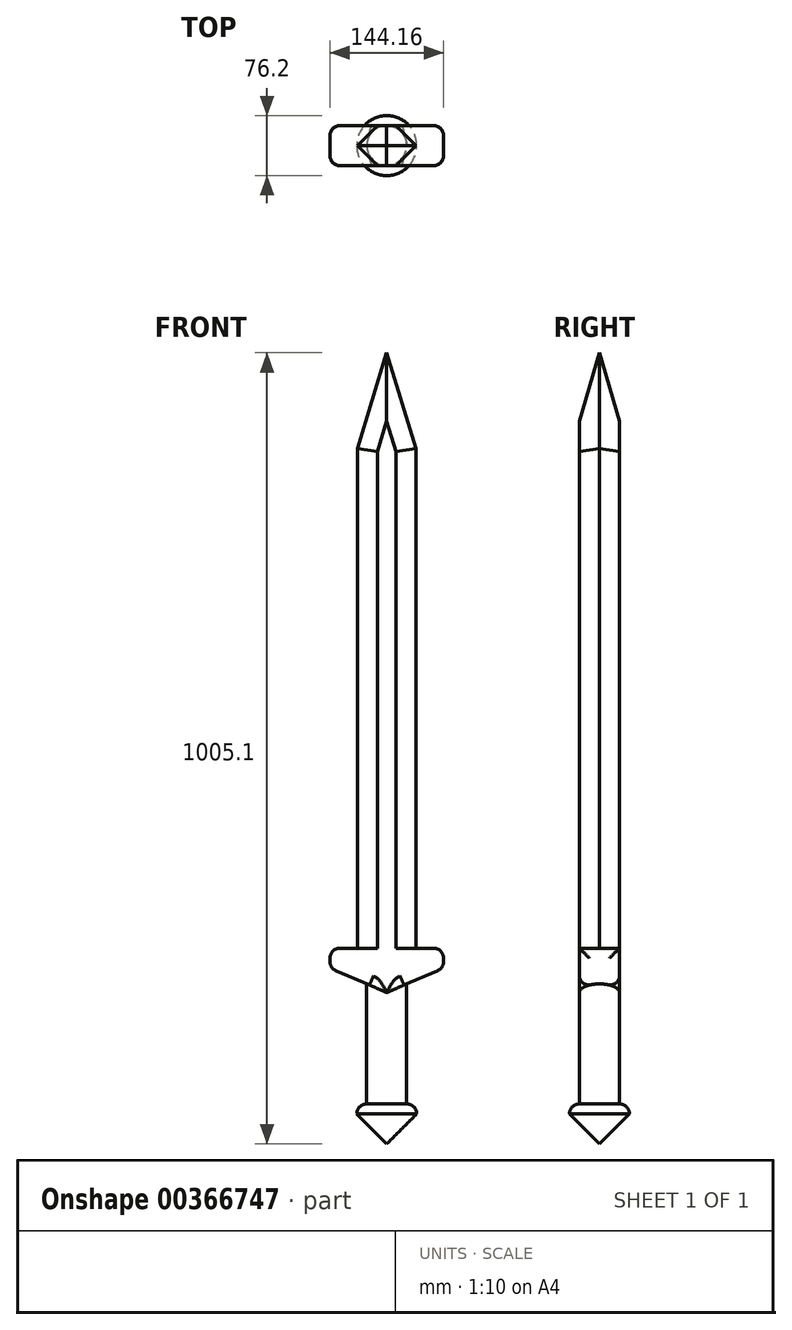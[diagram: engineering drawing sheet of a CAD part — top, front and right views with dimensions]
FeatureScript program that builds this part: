
annotation { "Feature Type Name" : "Feature", "Feature Type Description" : "" }
export const myFeature = defineFeature(function(context is Context, id is Id, definition is map)
    precondition{}
    {
        {
            var Q0;
            Q0=qCreatedBy(makeId("Front.planeOp"),FACE);
            var sketch = newSketch(context, id + "F0", { "sketchPlane" : qUnion([Q0])});
            skLineSegment(sketch, "E0.bottom", {"start": v(25.4, -76.2) * mm, "end": v(-25.4, -76.2) * mm});
            skLineSegment(sketch, "E0.top", {"start": v(25.4, 76.2) * mm, "end": v(-25.4, 76.2) * mm});
            skLineSegment(sketch, "E0.left", {"start": v(25.4, -76.2) * mm, "end": v(25.4, 76.2) * mm});
            skLineSegment(sketch, "E0.right", {"start": v(-25.4, -76.2) * mm, "end": v(-25.4, 76.2) * mm});
            skPoint(sketch, "E0.middle", {"position": v(0, 0) * mm});
            skSolve(sketch);
        }
        {
            var Q0;
            Q0 = qSketchRegion(id + "F0", true);
            extrude(context, id + "F1", {"entities" : qUnion([Q0]), "depth" : 50.8 * mm});
        }
        {
            var Q0;
            Q0=makeQuery(id+"F1.opExtrude","SWEPT_FACE",FACE,{"disambiguationData":[OSD([sQuery(id+"F0.wireOp",EDGE,"E0.bottom")])]});
            var sketch = newSketch(context, id + "F2", { "sketchPlane" : qUnion([Q0])});
            skLineSegment(sketch, "E1", {"start": v(0, 0) * mm, "end": v(0, 50.8) * mm});
            skLineSegment(sketch, "E2", {"start": v(0, 50.8) * mm, "end": v(0, 25.4) * mm});
            skCircle(sketch, "E3", {"center": v(0, 25.4) * mm, "radius": 38.1 * mm});
            skSolve(sketch);
        }
        {
            var Q0;
            Q0 = qSketchRegion(id + "F2", true);
            extrude(context, id + "F3", {"entities" : qUnion([Q0]), "operationType" : NewBodyOperationType.ADD, "depth" : 50.8 * mm});
        }
        {
            var Q0;
            Q0=makeQuery(id+"F1.opExtrude","CAP_FACE",FACE,{"disambiguationData":[OSD([sQuery(id+"F0.wireOp",EDGE,"E0.bottom"),sQuery(id+"F0.wireOp",EDGE,"E0.top"),sQuery(id+"F0.wireOp",EDGE,"E0.left"),sQuery(id+"F0.wireOp",EDGE,"E0.right")])],"isStart":false});
            var sketch = newSketch(context, id + "F4", { "sketchPlane" : qUnion([Q0])});
            skLineSegment(sketch, "E4", {"start": v(-25.4, 76.2) * mm, "end": v(-72.08, 96.23) * mm});
            skLineSegment(sketch, "E5", {"start": v(-72.08, 96.23) * mm, "end": v(-72.08, 121.63) * mm});
            skLineSegment(sketch, "E6", {"start": v(-72.08, 121.63) * mm, "end": v(0, 121.63) * mm});
            skLineSegment(sketch, "E7.MirrorCS", {"start": v(72.08, 121.63) * mm, "end": v(0, 121.63) * mm});
            skLineSegment(sketch, "E8.MirrorCS", {"start": v(72.08, 96.23) * mm, "end": v(72.08, 121.63) * mm});
            skLineSegment(sketch, "E9.MirrorCS", {"start": v(25.4, 76.2) * mm, "end": v(72.08, 96.23) * mm});
            skSolve(sketch);
        }
        {
            var Q0;
            Q0 = qSketchRegion(id + "F4", true);
            var Q1;
            Q1=makeQuery(id+"F4.imprint","IMPRINT",FACE,{"disambiguationData":[TD([[makeQuery(id+"F4.imprint","IMPRINT",EDGE,{"derivedFrom":sQuery(id+"F4.wireOp",EDGE,"E4")}),-1.0]])]});
            extrude(context, id + "F5", {"entities" : qUnion([Q0, Q1]), "operationType" : NewBodyOperationType.ADD, "depth" : -50.8 * mm});
        }
        {
            var Q0;
            {var subQ0=sQuery(id+"F0.wireOp",EDGE,"E0.top");Q0=makeQuery(id+"F5.boolean.opBoolean","MERGE",FACE,{"derivedFrom":[makeQuery(id+"F1.opExtrude","CAP_FACE",FACE,{"disambiguationData":[OSD([sQuery(id+"F0.wireOp",EDGE,"E0.bottom"),subQ0,sQuery(id+"F0.wireOp",EDGE,"E0.left"),sQuery(id+"F0.wireOp",EDGE,"E0.right")])],"isStart":true}),makeQuery(id+"F5.opExtrude","CAP_FACE",FACE,{"disambiguationData":[OSD([subQ0,sQuery(id+"F4.wireOp",EDGE,"E4"),sQuery(id+"F4.wireOp",EDGE,"E5"),sQuery(id+"F4.wireOp",EDGE,"E6"),sQuery(id+"F4.wireOp",EDGE,"E7.MirrorCS"),sQuery(id+"F4.wireOp",EDGE,"E8.MirrorCS"),sQuery(id+"F4.wireOp",EDGE,"E9.MirrorCS")])],"isStart":false})]});}
            var sketch = newSketch(context, id + "F6", { "sketchPlane" : qUnion([Q0])});
            skLineSegment(sketch, "E10", {"start": v(-25.4, 76.2) * mm, "end": v(-25.4, 121.63) * mm});
            skLineSegment(sketch, "E11", {"start": v(25.4, 76.2) * mm, "end": v(25.4, 121.63) * mm});
            skLineSegment(sketch, "E12", {"start": v(-25.4, 121.63) * mm, "end": v(-72.08, 121.63) * mm});
            skLineSegment(sketch, "E13", {"start": v(-72.08, 121.63) * mm, "end": v(-48.74, 121.63) * mm});
            skLineSegment(sketch, "E14", {"start": v(-48.74, 121.63) * mm, "end": v(25.4, 121.63) * mm});
            skLineSegment(sketch, "E15", {"start": v(25.4, 121.63) * mm, "end": v(72.08, 121.63) * mm});
            skLineSegment(sketch, "E16", {"start": v(72.08, 121.63) * mm, "end": v(48.74, 121.63) * mm});
            skLineSegment(sketch, "E17", {"start": v(25.4, 121.63) * mm, "end": v(48.74, 121.63) * mm});
            skLineSegment(sketch, "E18", {"start": v(37.07, 121.63) * mm, "end": v(-25.4, 121.63) * mm});
            skLineSegment(sketch, "E19", {"start": v(-25.4, 121.63) * mm, "end": v(-48.74, 121.63) * mm});
            skLineSegment(sketch, "E20", {"start": v(-48.74, 121.63) * mm, "end": v(-37.07, 121.63) * mm});
            skLineSegment(sketch, "E21", {"start": v(-37.07, 121.63) * mm, "end": v(-25.4, 121.63) * mm});
            skLineSegment(sketch, "E22", {"start": v(-37.07, 121.63) * mm, "end": v(-37.07, 756.63) * mm});
            skLineSegment(sketch, "E23", {"start": v(-37.07, 756.63) * mm, "end": v(0, 878.1) * mm});
            skLineSegment(sketch, "E24.MirrorCS", {"start": v(37.07, 756.63) * mm, "end": v(0, 878.1) * mm});
            skLineSegment(sketch, "E25.MirrorCS", {"start": v(37.07, 121.63) * mm, "end": v(37.07, 756.63) * mm});
            skSolve(sketch);
        }
        {
            var Q0;
            {var subQ0=sQuery(id+"F6.wireOp",EDGE,"PY2WEZBQ-7PR6-9Fpz-Vapi-aHdPcGGFADP5");Q0=makeQuery(id+"F6.imprint","IMPRINT",FACE,{"disambiguationData":[TD([[makeQuery(id+"F6.imprint","IMPRINT",EDGE,{"derivedFrom":subQ0}),-1.0]])]});}
            var Q1;
            {var subQ0=sQuery(id+"F6.wireOp",EDGE,"f0GTGxwF-IPFW-NOuP-a3Bc-MOuoexxvz6AO");Q1=makeQuery(id+"F6.imprint","IMPRINT",FACE,{"disambiguationData":[TD([[makeQuery(id+"F6.imprint","IMPRINT",EDGE,{"derivedFrom":subQ0}),-1.0]])]});}
            var Q2;
            {var subQ1=sQuery(id+"F6.wireOp",EDGE,"6nlB1FJk-VPpw-S0uW-v87S-9lklJtyhY6W3");Q2=makeQuery(id+"F6.imprint","IMPRINT",FACE,{"disambiguationData":[TD([[makeQuery(id+"F6.imprint","IMPRINT",EDGE,{"derivedFrom":subQ1}),1.0]])]});}
            var Q3;
            {var subQ0=sQuery(id+"F6.wireOp",EDGE,"Ocn70z9U-hdZD-j4XZ-LXAR-4gYBC23h8k5L");Q3=makeQuery(id+"F6.imprint","IMPRINT",FACE,{"disambiguationData":[TD([[makeQuery(id+"F6.imprint","IMPRINT",EDGE,{"derivedFrom":subQ0}),-1.0]])]});}
            var Q4;
            {var subQ1=sQuery(id+"F6.wireOp",EDGE,"E15");Q4=makeQuery(id+"F6.imprint","IMPRINT",FACE,{"disambiguationData":[TD([[makeQuery(id+"F6.imprint","IMPRINT",EDGE,{"derivedFrom":subQ1}),1.0]])]});}
            var Q5;
            {var subQ0=sQuery(id+"F6.wireOp",EDGE,"E21");Q5=makeQuery(id+"F6.imprint","IMPRINT",FACE,{"disambiguationData":[TD([[makeQuery(id+"F6.imprint","IMPRINT",EDGE,{"derivedFrom":subQ0}),1.0]])]});}
            extrude(context, id + "F7", {"entities" : qUnion([Q0, Q1, Q2, Q3, Q4, Q5]), "operationType" : NewBodyOperationType.ADD, "depth" : -50.8 * mm});
        }
        {
            var Q0;
            Q0=makeQuery(id+"F1.opExtrude","CAP_EDGE",EDGE,{"disambiguationData":[OSD([sQuery(id+"F0.wireOp",EDGE,"E0.right")])],"isStart":false});
            var Q1;
            Q1=makeQuery(id+"F1.opExtrude","CAP_EDGE",EDGE,{"disambiguationData":[OSD([sQuery(id+"F0.wireOp",EDGE,"E0.left")])],"isStart":false});
            var Q2;
            Q2=makeQuery(id+"F1.opExtrude","CAP_EDGE",EDGE,{"disambiguationData":[OSD([sQuery(id+"F0.wireOp",EDGE,"E0.left")])],"isStart":true});
            var Q3;
            Q3=makeQuery(id+"F1.opExtrude","CAP_EDGE",EDGE,{"disambiguationData":[OSD([sQuery(id+"F0.wireOp",EDGE,"E0.right")])],"isStart":true});
            fillet(context, id + "F8", {"entities" : qUnion([Q0, Q1, Q2, Q3]), "radius" : 25.4 * mm, "tangentPropagation" : true, "allowEdgeOverflow" : false});
        }
        {
            var Q0;
            Q0=makeQuery(id+"F3.opExtrude","CAP_EDGE",EDGE,{"disambiguationData":[OSD([sQuery(id+"F2.wireOp",EDGE,"E3")])],"isStart":true});
            fillet(context, id + "F9", {"entities" : qUnion([Q0]), "radius" : 12.7 * mm, "tangentPropagation" : true, "allowEdgeOverflow" : false});
        }
        {
            var Q0;
            Q0=makeQuery(id+"F3.opExtrude","CAP_EDGE",EDGE,{"disambiguationData":[OSD([sQuery(id+"F2.wireOp",EDGE,"E3")])],"isStart":false});
            chamfer(context, id + "F10", {"entities" : qUnion([Q0]), "width" : 38.1 * mm, "tangentPropagation" : true});
        }
        {
            var Q0;
            Q0=makeQuery(id+"F5.opExtrude","CAP_EDGE",EDGE,{"disambiguationData":[OSD([sQuery(id+"F4.wireOp",EDGE,"E5")])],"isStart":true});
            var Q1;
            Q1=makeQuery(id+"F5.opExtrude","CAP_EDGE",EDGE,{"disambiguationData":[OSD([sQuery(id+"F4.wireOp",EDGE,"E5")])],"isStart":false});
            var Q2;
            Q2=makeQuery(id+"F5.opExtrude","CAP_EDGE",EDGE,{"disambiguationData":[OSD([sQuery(id+"F4.wireOp",EDGE,"E8.MirrorCS")])],"isStart":true});
            var Q3;
            Q3=makeQuery(id+"F5.opExtrude","CAP_EDGE",EDGE,{"disambiguationData":[OSD([sQuery(id+"F4.wireOp",EDGE,"E8.MirrorCS")])],"isStart":false});
            var Q4;
            Q4=makeQuery(id+"F5.opExtrude","SWEPT_EDGE",EDGE,{"disambiguationData":[OSD([sQuery(id+"F4.wireOp",EDGE,"E8.MirrorCS"),sQuery(id+"F4.wireOp",EDGE,"E9.MirrorCS")])]});
            var Q5;
            Q5=makeQuery(id+"F5.opExtrude","SWEPT_EDGE",EDGE,{"disambiguationData":[OSD([sQuery(id+"F4.wireOp",EDGE,"E7.MirrorCS"),sQuery(id+"F4.wireOp",EDGE,"E8.MirrorCS")])]});
            var Q6;
            Q6=makeQuery(id+"F5.opExtrude","SWEPT_EDGE",EDGE,{"disambiguationData":[OSD([sQuery(id+"F4.wireOp",EDGE,"E4"),sQuery(id+"F4.wireOp",EDGE,"E5")])]});
            var Q7;
            Q7=makeQuery(id+"F5.opExtrude","SWEPT_EDGE",EDGE,{"disambiguationData":[OSD([sQuery(id+"F4.wireOp",EDGE,"E5"),sQuery(id+"F4.wireOp",EDGE,"E6")])]});
            var Q8;
            Q8=makeQuery(id+"F5.opExtrude","CAP_EDGE",EDGE,{"disambiguationData":[OSD([sQuery(id+"F4.wireOp",EDGE,"E4")])],"isStart":true});
            var Q9;
            Q9=makeQuery(id+"F5.opExtrude","CAP_EDGE",EDGE,{"disambiguationData":[OSD([sQuery(id+"F4.wireOp",EDGE,"E9.MirrorCS")])],"isStart":true});
            var Q10;
            Q10=makeQuery(id+"F5.opExtrude","CAP_EDGE",EDGE,{"disambiguationData":[OSD([sQuery(id+"F4.wireOp",EDGE,"E4")])],"isStart":false});
            var Q11;
            Q11=makeQuery(id+"F5.opExtrude","CAP_EDGE",EDGE,{"disambiguationData":[OSD([sQuery(id+"F4.wireOp",EDGE,"E9.MirrorCS")])],"isStart":false});
            fillet(context, id + "F11", {"entities" : qUnion([Q0, Q1, Q2, Q3, Q4, Q5, Q6, Q7, Q8, Q9, Q10, Q11]), "radius" : 12.7 * mm, "tangentPropagation" : true, "allowEdgeOverflow" : false});
        }
        {
            var Q0;
            Q0=makeQuery(id+"F7.opExtrude","CAP_EDGE",EDGE,{"disambiguationData":[OSD([sQuery(id+"F6.wireOp",EDGE,"E22")])],"isStart":true});
            var Q1;
            Q1=makeQuery(id+"F7.opExtrude","CAP_EDGE",EDGE,{"disambiguationData":[OSD([sQuery(id+"F6.wireOp",EDGE,"E25.MirrorCS")])],"isStart":true});
            var Q2;
            Q2=makeQuery(id+"F7.opExtrude","CAP_EDGE",EDGE,{"disambiguationData":[OSD([sQuery(id+"F6.wireOp",EDGE,"E24.MirrorCS")])],"isStart":true});
            var Q3;
            Q3=makeQuery(id+"F7.opExtrude","CAP_EDGE",EDGE,{"disambiguationData":[OSD([sQuery(id+"F6.wireOp",EDGE,"E23")])],"isStart":true});
            var Q4;
            Q4=makeQuery(id+"F7.opExtrude","CAP_EDGE",EDGE,{"disambiguationData":[OSD([sQuery(id+"F6.wireOp",EDGE,"E23")])],"isStart":false});
            var Q5;
            Q5=makeQuery(id+"F7.opExtrude","CAP_EDGE",EDGE,{"disambiguationData":[OSD([sQuery(id+"F6.wireOp",EDGE,"E22")])],"isStart":false});
            var Q6;
            Q6=makeQuery(id+"F7.opExtrude","CAP_EDGE",EDGE,{"disambiguationData":[OSD([sQuery(id+"F6.wireOp",EDGE,"E24.MirrorCS")])],"isStart":false});
            var Q7;
            Q7=makeQuery(id+"F7.opExtrude","CAP_EDGE",EDGE,{"disambiguationData":[OSD([sQuery(id+"F6.wireOp",EDGE,"E25.MirrorCS")])],"isStart":false});
            chamfer(context, id + "F12", {"entities" : qUnion([Q0, Q1, Q2, Q3, Q4, Q5, Q6, Q7]), "chamferType" : ChamferType.OFFSET_ANGLE, "width" : 25.4 * mm, "oppositeDirection" : false, "angle" : 45 * degree, "tangentPropagation" : true});
        }
    });
